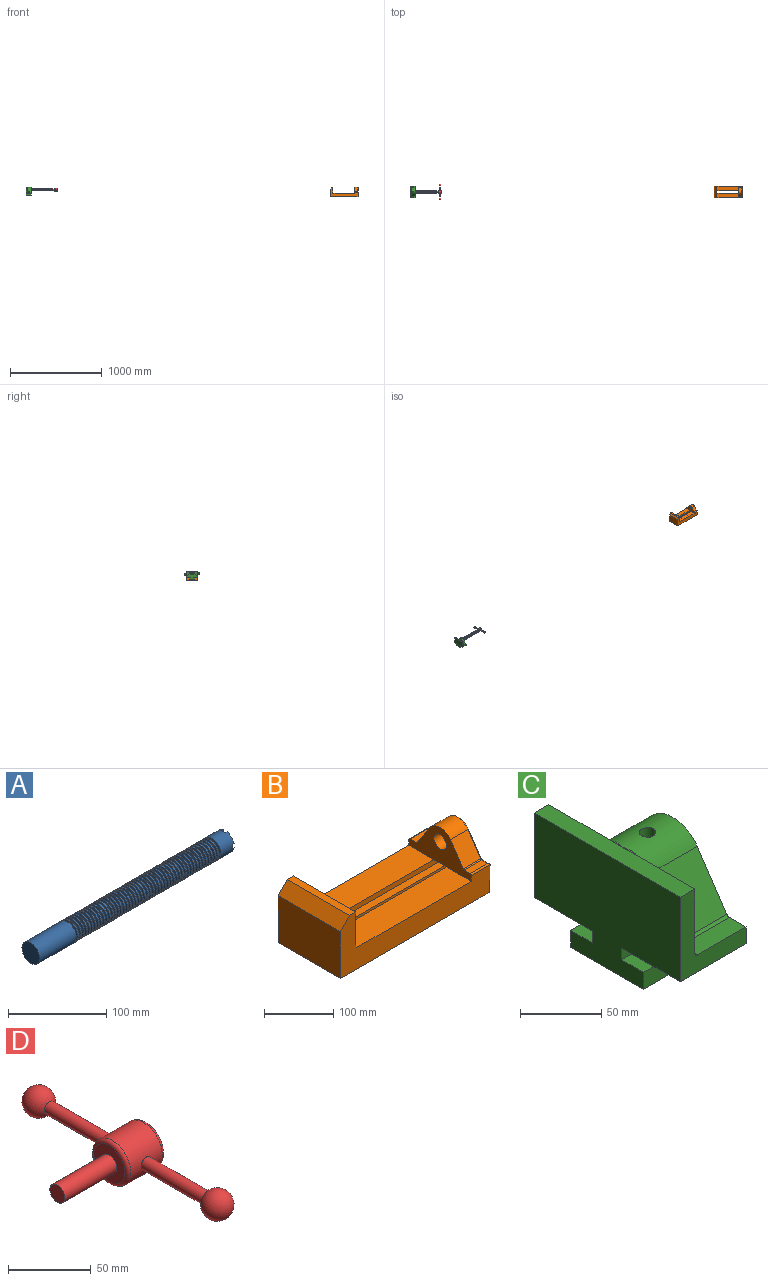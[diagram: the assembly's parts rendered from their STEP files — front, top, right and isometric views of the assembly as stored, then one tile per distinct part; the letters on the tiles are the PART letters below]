
ASSEMBLY  parts=4 mates=3
PART A: 220 faces, bbox 279.4x25.4x25.4 mm
  f0: cylinder r=12.7mm len=25.4mm, axis (-1,0,0), area 1468.2mm2, adj f1,f2,f3,f5,f7,f208,f209,f210
  f1: plane 9.9x9.9mm, normal (1,0,0), area 62.3mm2, adj f0,f4,f213,f216
  f2: plane 9.9x9.9mm, normal (1,0,0), area 62.3mm2, adj f0,f4,f210,f218
  f3: plane 9.9x9.9mm, normal (1,0,0), area 62.3mm2, adj f0,f4,f209,f212
  f4: cylinder r=6.35mm len=25.4mm, axis (1,0,0), area 960.3mm2, adj f1,f2,f3,f5,f6,f208,f209,f210
  f5: plane 9.9x9.9mm, normal (1,0,0), area 62.3mm2, adj f0,f4,f215,f217
  f6: plane 12.7x12.7mm, normal (1,0,0), area 126.7mm2, adj f4
  f7: cone r=12.7mm half-angle=76deg, axis (1,0,0), area 188mm2, adj f0,f9
  f8: cone r=10.16mm half-angle=76deg, axis (-1,0,0), area 188mm2, adj f9,f10
  f9: cylinder r=10.16mm len=20.32mm, axis (1,0,0), area 81.1mm2, adj f7,f8
  f10: cylinder r=12.7mm len=25.4mm, axis (-1,0,0), area 131.7mm2, adj f8,f11
  f11: cone r=12.7mm half-angle=76deg, axis (1,0,0), area 188mm2, adj f10,f13
  f12: cone r=10.16mm half-angle=76deg, axis (-1,0,0), area 188mm2, adj f13,f14
  f13: cylinder r=10.16mm len=20.32mm, axis (1,0,0), area 81.1mm2, adj f11,f12
  f14: cylinder r=12.7mm len=25.4mm, axis (-1,0,0), area 131.7mm2, adj f12,f15
  f15: cone r=12.7mm half-angle=76deg, axis (1,0,0), area 188mm2, adj f14,f17
  f16: cone r=10.16mm half-angle=76deg, axis (-1,0,0), area 188mm2, adj f17,f18
  f17: cylinder r=10.16mm len=20.32mm, axis (1,0,0), area 81.1mm2, adj f15,f16
  f18: cylinder r=12.7mm len=25.4mm, axis (-1,0,0), area 131.7mm2, adj f16,f19
  f19: cone r=12.7mm half-angle=76deg, axis (1,0,0), area 188mm2, adj f18,f21
  f20: cone r=10.16mm half-angle=76deg, axis (-1,0,0), area 188mm2, adj f21,f22
  f21: cylinder r=10.16mm len=20.32mm, axis (1,0,0), area 81.1mm2, adj f19,f20
  f22: cylinder r=12.7mm len=25.4mm, axis (-1,0,0), area 131.7mm2, adj f20,f23
  f23: cone r=12.7mm half-angle=76deg, axis (1,0,0), area 188mm2, adj f22,f25
  f24: cone r=10.16mm half-angle=76deg, axis (-1,0,0), area 188mm2, adj f25,f26
  f25: cylinder r=10.16mm len=20.32mm, axis (1,0,0), area 81.1mm2, adj f23,f24
  f26: cylinder r=12.7mm len=25.4mm, axis (-1,0,0), area 131.7mm2, adj f24,f27
  f27: cone r=12.7mm half-angle=76deg, axis (1,0,0), area 188mm2, adj f26,f29
  f28: cone r=10.16mm half-angle=76deg, axis (-1,0,0), area 188mm2, adj f29,f30
  f29: cylinder r=10.16mm len=20.32mm, axis (1,0,0), area 81.1mm2, adj f27,f28
  f30: cylinder r=12.7mm len=25.4mm, axis (-1,0,0), area 131.7mm2, adj f28,f31
  f31: cone r=12.7mm half-angle=76deg, axis (1,0,0), area 188mm2, adj f30,f33
  f32: cone r=10.16mm half-angle=76deg, axis (-1,0,0), area 188mm2, adj f33,f34
  f33: cylinder r=10.16mm len=20.32mm, axis (1,0,0), area 81.1mm2, adj f31,f32
  f34: cylinder r=12.7mm len=25.4mm, axis (-1,0,0), area 131.7mm2, adj f32,f35
  f35: cone r=12.7mm half-angle=76deg, axis (1,0,0), area 188mm2, adj f34,f37
  f36: cone r=10.16mm half-angle=76deg, axis (-1,0,0), area 188mm2, adj f37,f38
  f37: cylinder r=10.16mm len=20.32mm, axis (1,0,0), area 81.1mm2, adj f35,f36
  f38: cylinder r=12.7mm len=25.4mm, axis (-1,0,0), area 131.7mm2, adj f36,f39
  f39: cone r=12.7mm half-angle=76deg, axis (1,0,0), area 188mm2, adj f38,f41
  f40: cone r=10.16mm half-angle=76deg, axis (-1,0,0), area 188mm2, adj f41,f42
  f41: cylinder r=10.16mm len=20.32mm, axis (1,0,0), area 81.1mm2, adj f39,f40
  f42: cylinder r=12.7mm len=25.4mm, axis (-1,0,0), area 131.7mm2, adj f40,f43
  f43: cone r=12.7mm half-angle=76deg, axis (1,0,0), area 188mm2, adj f42,f45
  f44: cone r=10.16mm half-angle=76deg, axis (-1,0,0), area 188mm2, adj f45,f46
  f45: cylinder r=10.16mm len=20.32mm, axis (1,0,0), area 81.1mm2, adj f43,f44
  f46: cylinder r=12.7mm len=25.4mm, axis (-1,0,0), area 131.7mm2, adj f44,f47
  f47: cone r=12.7mm half-angle=76deg, axis (1,0,0), area 188mm2, adj f46,f49
  f48: cone r=10.16mm half-angle=76deg, axis (-1,0,0), area 188mm2, adj f49,f50
  f49: cylinder r=10.16mm len=20.32mm, axis (1,0,0), area 81.1mm2, adj f47,f48
  f50: cylinder r=12.7mm len=25.4mm, axis (-1,0,0), area 131.7mm2, adj f48,f51
  f51: cone r=12.7mm half-angle=76deg, axis (1,0,0), area 188mm2, adj f50,f53
  f52: cone r=10.16mm half-angle=76deg, axis (-1,0,0), area 188mm2, adj f53,f54
  f53: cylinder r=10.16mm len=20.32mm, axis (1,0,0), area 81.1mm2, adj f51,f52
  f54: cylinder r=12.7mm len=25.4mm, axis (-1,0,0), area 131.7mm2, adj f52,f55
  f55: cone r=12.7mm half-angle=76deg, axis (1,0,0), area 188mm2, adj f54,f57
  f56: cone r=10.16mm half-angle=76deg, axis (-1,0,0), area 188mm2, adj f57,f58
  f57: cylinder r=10.16mm len=20.32mm, axis (1,0,0), area 81.1mm2, adj f55,f56
  f58: cylinder r=12.7mm len=25.4mm, axis (-1,0,0), area 131.7mm2, adj f56,f59
  f59: cone r=12.7mm half-angle=76deg, axis (1,0,0), area 188mm2, adj f58,f61
  f60: cone r=10.16mm half-angle=76deg, axis (-1,0,0), area 188mm2, adj f61,f62
  f61: cylinder r=10.16mm len=20.32mm, axis (1,0,0), area 81.1mm2, adj f59,f60
  f62: cylinder r=12.7mm len=25.4mm, axis (-1,0,0), area 131.7mm2, adj f60,f63
  f63: cone r=12.7mm half-angle=76deg, axis (1,0,0), area 188mm2, adj f62,f65
  f64: cone r=10.16mm half-angle=76deg, axis (-1,0,0), area 188mm2, adj f65,f66
  f65: cylinder r=10.16mm len=20.32mm, axis (1,0,0), area 81.1mm2, adj f63,f64
  f66: cylinder r=12.7mm len=25.4mm, axis (-1,0,0), area 131.7mm2, adj f64,f67
  f67: cone r=12.7mm half-angle=76deg, axis (1,0,0), area 188mm2, adj f66,f69
  f68: cone r=10.16mm half-angle=76deg, axis (-1,0,0), area 188mm2, adj f69,f70
  f69: cylinder r=10.16mm len=20.32mm, axis (1,0,0), area 81.1mm2, adj f67,f68
  f70: cylinder r=12.7mm len=25.4mm, axis (-1,0,0), area 131.7mm2, adj f68,f71
  f71: cone r=12.7mm half-angle=76deg, axis (1,0,0), area 188mm2, adj f70,f73
  f72: cone r=10.16mm half-angle=76deg, axis (-1,0,0), area 188mm2, adj f73,f74
  f73: cylinder r=10.16mm len=20.32mm, axis (1,0,0), area 81.1mm2, adj f71,f72
  f74: cylinder r=12.7mm len=25.4mm, axis (-1,0,0), area 131.7mm2, adj f72,f75
  f75: cone r=12.7mm half-angle=76deg, axis (1,0,0), area 188mm2, adj f74,f77
  f76: cone r=10.16mm half-angle=76deg, axis (-1,0,0), area 188mm2, adj f77,f78
  f77: cylinder r=10.16mm len=20.32mm, axis (1,0,0), area 81.1mm2, adj f75,f76
  f78: cylinder r=12.7mm len=25.4mm, axis (-1,0,0), area 131.7mm2, adj f76,f79
  f79: cone r=12.7mm half-angle=76deg, axis (1,0,0), area 188mm2, adj f78,f81
  f80: cone r=10.16mm half-angle=76deg, axis (-1,0,0), area 188mm2, adj f81,f82
  f81: cylinder r=10.16mm len=20.32mm, axis (1,0,0), area 81.1mm2, adj f79,f80
  f82: cylinder r=12.7mm len=25.4mm, axis (-1,0,0), area 131.7mm2, adj f80,f83
  f83: cone r=12.7mm half-angle=76deg, axis (1,0,0), area 188mm2, adj f82,f85
  f84: cone r=10.16mm half-angle=76deg, axis (-1,0,0), area 188mm2, adj f85,f86
  f85: cylinder r=10.16mm len=20.32mm, axis (1,0,0), area 81.1mm2, adj f83,f84
  f86: cylinder r=12.7mm len=25.4mm, axis (-1,0,0), area 131.7mm2, adj f84,f87
  f87: cone r=12.7mm half-angle=76deg, axis (1,0,0), area 188mm2, adj f86,f89
  f88: cone r=10.16mm half-angle=76deg, axis (-1,0,0), area 188mm2, adj f89,f90
  f89: cylinder r=10.16mm len=20.32mm, axis (1,0,0), area 81.1mm2, adj f87,f88
  f90: cylinder r=12.7mm len=25.4mm, axis (-1,0,0), area 131.7mm2, adj f88,f91
  f91: cone r=12.7mm half-angle=76deg, axis (1,0,0), area 188mm2, adj f90,f93
  f92: cone r=10.16mm half-angle=76deg, axis (-1,0,0), area 188mm2, adj f93,f94
  f93: cylinder r=10.16mm len=20.32mm, axis (1,0,0), area 81.1mm2, adj f91,f92
  f94: cylinder r=12.7mm len=25.4mm, axis (-1,0,0), area 131.7mm2, adj f92,f95
  f95: cone r=12.7mm half-angle=76deg, axis (1,0,0), area 188mm2, adj f94,f97
  f96: cone r=10.16mm half-angle=76deg, axis (-1,0,0), area 188mm2, adj f97,f98
  f97: cylinder r=10.16mm len=20.32mm, axis (1,0,0), area 81.1mm2, adj f95,f96
  f98: cylinder r=12.7mm len=25.4mm, axis (-1,0,0), area 131.7mm2, adj f96,f99
  f99: cone r=12.7mm half-angle=76deg, axis (1,0,0), area 188mm2, adj f98,f101
  f100: cone r=10.16mm half-angle=76deg, axis (-1,0,0), area 188mm2, adj f101,f102
  f101: cylinder r=10.16mm len=20.32mm, axis (1,0,0), area 81.1mm2, adj f99,f100
  f102: cylinder r=12.7mm len=25.4mm, axis (-1,0,0), area 131.7mm2, adj f100,f103
  f103: cone r=12.7mm half-angle=76deg, axis (1,0,0), area 188mm2, adj f102,f105
  f104: cone r=10.16mm half-angle=76deg, axis (-1,0,0), area 188mm2, adj f105,f106
  f105: cylinder r=10.16mm len=20.32mm, axis (1,0,0), area 81.1mm2, adj f103,f104
  f106: cylinder r=12.7mm len=25.4mm, axis (-1,0,0), area 131.7mm2, adj f104,f107
  f107: cone r=12.7mm half-angle=76deg, axis (1,0,0), area 188mm2, adj f106,f109
  f108: cone r=10.16mm half-angle=76deg, axis (-1,0,0), area 188mm2, adj f109,f110
  f109: cylinder r=10.16mm len=20.32mm, axis (1,0,0), area 81.1mm2, adj f107,f108
  f110: cylinder r=12.7mm len=25.4mm, axis (-1,0,0), area 131.7mm2, adj f108,f111
  f111: cone r=12.7mm half-angle=76deg, axis (1,0,0), area 188mm2, adj f110,f113
  f112: cone r=10.16mm half-angle=76deg, axis (-1,0,0), area 188mm2, adj f113,f114
  f113: cylinder r=10.16mm len=20.32mm, axis (1,0,0), area 81.1mm2, adj f111,f112
  f114: cylinder r=12.7mm len=25.4mm, axis (-1,0,0), area 131.7mm2, adj f112,f115
  f115: cone r=12.7mm half-angle=76deg, axis (1,0,0), area 188mm2, adj f114,f117
  f116: cone r=10.16mm half-angle=76deg, axis (-1,0,0), area 188mm2, adj f117,f118
  f117: cylinder r=10.16mm len=20.32mm, axis (1,0,0), area 81.1mm2, adj f115,f116
  f118: cylinder r=12.7mm len=25.4mm, axis (-1,0,0), area 131.7mm2, adj f116,f119
  f119: cone r=12.7mm half-angle=76deg, axis (1,0,0), area 188mm2, adj f118,f121
  f120: cone r=10.16mm half-angle=76deg, axis (-1,0,0), area 188mm2, adj f121,f122
  f121: cylinder r=10.16mm len=20.32mm, axis (1,0,0), area 81.1mm2, adj f119,f120
  f122: cylinder r=12.7mm len=25.4mm, axis (-1,0,0), area 131.7mm2, adj f120,f123
  f123: cone r=12.7mm half-angle=76deg, axis (1,0,0), area 188mm2, adj f122,f125
  f124: cone r=10.16mm half-angle=76deg, axis (-1,0,0), area 188mm2, adj f125,f126
  f125: cylinder r=10.16mm len=20.32mm, axis (1,0,0), area 81.1mm2, adj f123,f124
  f126: cylinder r=12.7mm len=25.4mm, axis (-1,0,0), area 131.7mm2, adj f124,f127
  f127: cone r=12.7mm half-angle=76deg, axis (1,0,0), area 188mm2, adj f126,f129
  f128: cone r=10.16mm half-angle=76deg, axis (-1,0,0), area 188mm2, adj f129,f130
  f129: cylinder r=10.16mm len=20.32mm, axis (1,0,0), area 81.1mm2, adj f127,f128
  f130: cylinder r=12.7mm len=25.4mm, axis (-1,0,0), area 131.7mm2, adj f128,f131
  f131: cone r=12.7mm half-angle=76deg, axis (1,0,0), area 188mm2, adj f130,f133
  f132: cone r=10.16mm half-angle=76deg, axis (-1,0,0), area 188mm2, adj f133,f134
  f133: cylinder r=10.16mm len=20.32mm, axis (1,0,0), area 81.1mm2, adj f131,f132
  f134: cylinder r=12.7mm len=25.4mm, axis (-1,0,0), area 131.7mm2, adj f132,f135
  f135: cone r=12.7mm half-angle=76deg, axis (1,0,0), area 188mm2, adj f134,f137
  f136: cone r=10.16mm half-angle=76deg, axis (-1,0,0), area 188mm2, adj f137,f138
  f137: cylinder r=10.16mm len=20.32mm, axis (1,0,0), area 81.1mm2, adj f135,f136
  f138: cylinder r=12.7mm len=25.4mm, axis (-1,0,0), area 131.7mm2, adj f136,f139
  f139: cone r=12.7mm half-angle=76deg, axis (1,0,0), area 188mm2, adj f138,f141
  f140: cone r=10.16mm half-angle=76deg, axis (-1,0,0), area 188mm2, adj f141,f142
  f141: cylinder r=10.16mm len=20.32mm, axis (1,0,0), area 81.1mm2, adj f139,f140
  f142: cylinder r=12.7mm len=25.4mm, axis (-1,0,0), area 131.7mm2, adj f140,f143
  f143: cone r=12.7mm half-angle=76deg, axis (1,0,0), area 188mm2, adj f142,f145
  f144: cone r=10.16mm half-angle=76deg, axis (-1,0,0), area 188mm2, adj f145,f146
  f145: cylinder r=10.16mm len=20.32mm, axis (1,0,0), area 81.1mm2, adj f143,f144
  f146: cylinder r=12.7mm len=25.4mm, axis (-1,0,0), area 131.7mm2, adj f144,f147
  f147: cone r=12.7mm half-angle=76deg, axis (1,0,0), area 188mm2, adj f146,f149
  f148: cone r=10.16mm half-angle=76deg, axis (-1,0,0), area 188mm2, adj f149,f150
  f149: cylinder r=10.16mm len=20.32mm, axis (1,0,0), area 81.1mm2, adj f147,f148
  f150: cylinder r=12.7mm len=25.4mm, axis (-1,0,0), area 131.7mm2, adj f148,f151
  f151: cone r=12.7mm half-angle=76deg, axis (1,0,0), area 188mm2, adj f150,f153
  f152: cone r=10.16mm half-angle=76deg, axis (-1,0,0), area 188mm2, adj f153,f154
  f153: cylinder r=10.16mm len=20.32mm, axis (1,0,0), area 81.1mm2, adj f151,f152
  f154: cylinder r=12.7mm len=25.4mm, axis (-1,0,0), area 131.7mm2, adj f152,f155
  f155: cone r=12.7mm half-angle=76deg, axis (1,0,0), area 188mm2, adj f154,f157
  f156: cone r=10.16mm half-angle=76deg, axis (-1,0,0), area 188mm2, adj f157,f158
  f157: cylinder r=10.16mm len=20.32mm, axis (1,0,0), area 81.1mm2, adj f155,f156
  f158: cylinder r=12.7mm len=25.4mm, axis (-1,0,0), area 131.7mm2, adj f156,f159
  f159: cone r=12.7mm half-angle=76deg, axis (1,0,0), area 188mm2, adj f158,f161
  f160: cone r=10.16mm half-angle=76deg, axis (-1,0,0), area 188mm2, adj f161,f162
  f161: cylinder r=10.16mm len=20.32mm, axis (1,0,0), area 81.1mm2, adj f159,f160
  f162: cylinder r=12.7mm len=25.4mm, axis (-1,0,0), area 131.7mm2, adj f160,f163
  f163: cone r=12.7mm half-angle=76deg, axis (1,0,0), area 188mm2, adj f162,f165
  f164: cone r=10.16mm half-angle=76deg, axis (-1,0,0), area 188mm2, adj f165,f166
  f165: cylinder r=10.16mm len=20.32mm, axis (1,0,0), area 81.1mm2, adj f163,f164
  f166: cylinder r=12.7mm len=25.4mm, axis (-1,0,0), area 131.7mm2, adj f164,f167
  f167: cone r=12.7mm half-angle=76deg, axis (1,0,0), area 188mm2, adj f166,f169
  f168: cone r=10.16mm half-angle=76deg, axis (-1,0,0), area 188mm2, adj f169,f170
  f169: cylinder r=10.16mm len=20.32mm, axis (1,0,0), area 81.1mm2, adj f167,f168
  f170: cylinder r=12.7mm len=25.4mm, axis (-1,0,0), area 131.7mm2, adj f168,f171
  f171: cone r=12.7mm half-angle=76deg, axis (1,0,0), area 188mm2, adj f170,f173
  f172: cone r=10.16mm half-angle=76deg, axis (-1,0,0), area 188mm2, adj f173,f174
  f173: cylinder r=10.16mm len=20.32mm, axis (1,0,0), area 81.1mm2, adj f171,f172
  f174: cylinder r=12.7mm len=25.4mm, axis (-1,0,0), area 131.7mm2, adj f172,f175
  f175: cone r=12.7mm half-angle=76deg, axis (1,0,0), area 188mm2, adj f174,f177
  f176: cone r=10.16mm half-angle=76deg, axis (-1,0,0), area 188mm2, adj f177,f178
  f177: cylinder r=10.16mm len=20.32mm, axis (1,0,0), area 81.1mm2, adj f175,f176
  f178: cylinder r=12.7mm len=25.4mm, axis (-1,0,0), area 131.7mm2, adj f176,f179
  f179: cone r=12.7mm half-angle=76deg, axis (1,0,0), area 188mm2, adj f178,f181
  f180: cone r=10.16mm half-angle=76deg, axis (-1,0,0), area 188mm2, adj f181,f182
  f181: cylinder r=10.16mm len=20.32mm, axis (1,0,0), area 81.1mm2, adj f179,f180
  f182: cylinder r=12.7mm len=25.4mm, axis (-1,0,0), area 131.7mm2, adj f180,f183
  f183: cone r=12.7mm half-angle=76deg, axis (1,0,0), area 188mm2, adj f182,f185
  f184: cone r=10.16mm half-angle=76deg, axis (-1,0,0), area 188mm2, adj f185,f186
  f185: cylinder r=10.16mm len=20.32mm, axis (1,0,0), area 81.1mm2, adj f183,f184
  f186: cylinder r=12.7mm len=25.4mm, axis (-1,0,0), area 131.7mm2, adj f184,f187
  f187: cone r=12.7mm half-angle=76deg, axis (1,0,0), area 188mm2, adj f186,f189
  f188: cone r=10.16mm half-angle=76deg, axis (-1,0,0), area 188mm2, adj f189,f190
  f189: cylinder r=10.16mm len=20.32mm, axis (1,0,0), area 81.1mm2, adj f187,f188
  f190: cylinder r=12.7mm len=25.4mm, axis (-1,0,0), area 131.7mm2, adj f188,f191
  f191: cone r=12.7mm half-angle=76deg, axis (1,0,0), area 188mm2, adj f190,f193
  f192: cone r=10.16mm half-angle=76deg, axis (-1,0,0), area 188mm2, adj f193,f194
  f193: cylinder r=10.16mm len=20.32mm, axis (1,0,0), area 81.1mm2, adj f191,f192
  f194: cylinder r=12.7mm len=25.4mm, axis (-1,0,0), area 131.7mm2, adj f192,f195
  f195: cone r=12.7mm half-angle=76deg, axis (1,0,0), area 188mm2, adj f194,f197
  f196: cone r=10.16mm half-angle=76deg, axis (-1,0,0), area 188mm2, adj f197,f198
  f197: cylinder r=10.16mm len=20.32mm, axis (1,0,0), area 81.1mm2, adj f195,f196
  f198: cylinder r=12.7mm len=25.4mm, axis (-1,0,0), area 131.7mm2, adj f196,f199
  f199: cone r=12.7mm half-angle=76deg, axis (1,0,0), area 188mm2, adj f198,f201
  f200: cone r=10.16mm half-angle=76deg, axis (-1,0,0), area 188mm2, adj f201,f202
  f201: cylinder r=10.16mm len=20.32mm, axis (1,0,0), area 81.1mm2, adj f199,f200
  f202: cylinder r=12.7mm len=25.4mm, axis (-1,0,0), area 131.7mm2, adj f200,f203
  f203: cone r=12.7mm half-angle=76deg, axis (1,0,0), area 188mm2, adj f202,f205
  f204: cone r=10.16mm half-angle=76deg, axis (-1,0,0), area 188mm2, adj f205,f207
  f205: cylinder r=10.16mm len=20.32mm, axis (1,0,0), area 81.1mm2, adj f203,f204
  f206: plane 25.4x25.4mm, normal (-1,0,0), area 506.7mm2, adj f207
  f207: cylinder r=12.7mm len=52.45mm, axis (-1,0,0), area 4185.4mm2, adj f204,f206
  f208: plane 6.88x5.08mm, normal (1,0,0), area 32.7mm2, adj f0,f4,f209,f210
  f209: plane 6.62x2.54mm, normal (0,-1,0), area 16.8mm2, adj f0,f3,f4,f208
  f210: plane 6.62x2.54mm, normal (0,1,0), area 16.8mm2, adj f0,f2,f4,f208
  f211: plane 6.88x5.08mm, normal (1,0,0), area 32.7mm2, adj f0,f4,f212,f213
  f212: plane 6.62x2.54mm, normal (0,0,1), area 16.8mm2, adj f0,f3,f4,f211
  f213: plane 6.62x2.54mm, normal (0,0,-1), area 16.8mm2, adj f0,f1,f4,f211
  f214: plane 6.88x5.08mm, normal (1,0,0), area 32.7mm2, adj f0,f4,f215,f216
  f215: plane 6.62x2.54mm, normal (0,1,0), area 16.8mm2, adj f0,f4,f5,f214
  f216: plane 6.62x2.54mm, normal (0,-1,0), area 16.8mm2, adj f0,f1,f4,f214
  f217: plane 6.62x2.54mm, normal (0,0,-1), area 16.8mm2, adj f0,f4,f5,f219
  f218: plane 6.62x2.54mm, normal (0,0,1), area 16.8mm2, adj f0,f2,f4,f219
  f219: plane 6.88x5.08mm, normal (1,0,0), area 32.7mm2, adj f0,f4,f217,f218
PART B: 39 faces, bbox 304.8x127x103.7 mm
  f0: plane 234.95x50.8mm, normal (0,0,1), area 11935.5mm2, adj f2,f8,f16,f26
  f1: plane 234.95x50.8mm, normal (0,0,1), area 11935.5mm2, adj f2,f9,f16,f27
  f2: plane 127x101.6mm, normal (1,0,0), area 9516.1mm2, adj f0,f1,f3,f6,f8,f9,f18,f19
  f3: plane 127x12.7mm, normal (0,0,1), area 1612.9mm2, adj f2,f4,f8,f9
  f4: plane 127x19.05mm, normal (-0.71,0,0.71), area 3421.5mm2, adj f3,f5,f8,f9
  f5: plane 127x82.55mm, normal (-1,0,0), area 10483.9mm2, adj f4,f6,f8,f9
  f6: plane 304.8x127mm, normal (0,0,-1), area 31774.1mm2, adj f2,f5,f7,f8,f9,f21,f22
  f7: plane 127x99.06mm, normal (1,0,0), area 7097.5mm2, adj f6,f8,f9,f14,f17,f18,f19,f20
  f8: plane 304.8x101.6mm, normal (0,-1,0), area 13834.6mm2, adj f0,f2,f3,f4,f5,f6,f7,f16
  f9: plane 304.8x101.6mm, normal (0,1,0), area 13834.6mm2, adj f1,f2,f3,f4,f5,f6,f7,f16
  f10: plane 35.56x11.98mm, normal (0,0,1), area 426mm2, adj f16,f28,f29,f30
  f11: plane 38.43x35.56mm, normal (0,0.83,0.56), area 1645.4mm2, adj f12,f16,f29,f32
  f12: cylinder r=25.4mm len=42.19mm, axis (1,0,0), area 1770.2mm2, adj f11,f13,f16,f33
  f13: plane 38.43x35.56mm, normal (0,-0.83,0.56), area 1645.4mm2, adj f12,f16,f34,f35
  f14: cylinder r=12.7mm len=38.1mm, axis (1,0,0), area 3040.2mm2, adj f7,f16
  f15: plane 35.56x11.98mm, normal (0,0,1), area 426mm2, adj f16,f34,f36,f38
  f16: plane 127x63.5mm, normal (-1,0,0), area 4155.5mm2, adj f0,f1,f8,f9,f10,f11,f12,f13
  f17: plane 38.1x25.4mm, normal (0,0,-1), area 967.7mm2, adj f7,f16,f26,f27
  f18: plane 273.05x19.05mm, normal (0,0,-1), area 5201.6mm2, adj f2,f7,f19,f26
  f19: plane 273.05x12.7mm, normal (0,1,0), area 3467.7mm2, adj f2,f7,f18,f20
  f20: plane 273.05x19.05mm, normal (0,0,1), area 5201.6mm2, adj f2,f7,f19,f21
  f21: plane 273.05x16.51mm, normal (0,1,0), area 4508.1mm2, adj f2,f6,f7,f20
  f22: plane 273.05x16.51mm, normal (0,-1,0), area 4508.1mm2, adj f2,f6,f7,f23
  f23: plane 273.05x19.05mm, normal (0,0,1), area 5201.6mm2, adj f2,f7,f22,f24
  f24: plane 273.05x12.7mm, normal (0,-1,0), area 3467.7mm2, adj f2,f7,f23,f25
  f25: plane 273.05x19.05mm, normal (0,0,-1), area 5201.6mm2, adj f2,f7,f24,f27
  f26: plane 273.05x8.89mm, normal (0,1,0), area 2427.4mm2, adj f0,f2,f7,f17,f18
  f27: plane 273.05x8.89mm, normal (0,-1,0), area 2427.4mm2, adj f1,f2,f7,f17,f25
  f28: cylinder r=2.54mm len=38.1mm, axis (1,0,0), area 148.3mm2, adj f9,f10,f16,f30
  f29: cylinder r=2.54mm len=35.56mm, axis (-1,0,0), area 88.5mm2, adj f10,f11,f16,f31
  f30: cylinder r=2.54mm len=14.52mm, axis (0,1,0), area 54.3mm2, adj f7,f10,f28,f31
  f31: torus R=5.08mm, axis (-1,0,0), area 13.5mm2, adj f7,f29,f30,f32
  f32: cylinder r=2.54mm len=39.84mm, axis (0,0.56,-0.83), area 184.6mm2, adj f7,f11,f31,f33
  f33: torus R=22.86mm, axis (-1,0,0), area 191.4mm2, adj f7,f12,f32,f35
  f34: cylinder r=2.54mm len=35.56mm, axis (-1,0,0), area 88.5mm2, adj f13,f15,f16,f37
  f35: cylinder r=2.54mm len=39.84mm, axis (0,0.56,0.83), area 184.6mm2, adj f7,f13,f33,f37
  f36: cylinder r=2.54mm len=38.1mm, axis (-1,0,0), area 148.3mm2, adj f8,f15,f16,f38
  f37: torus R=5.08mm, axis (-1,0,0), area 13.5mm2, adj f7,f34,f35,f38
  f38: cylinder r=2.54mm len=14.52mm, axis (0,1,0), area 54.3mm2, adj f7,f15,f36,f37
PART C: 36 faces, bbox 57.2x127x89 mm
  f0: plane 57.15x50.8mm, normal (0,0,-1), area 2903.2mm2, adj f6,f9,f10,f23
  f1: cylinder r=12.7mm len=44.45mm, axis (1,0,0), area 3464.3mm2, adj f6,f15,f16
  f2: plane 41.91x14.52mm, normal (0,0,1), area 608.5mm2, adj f6,f11,f24,f25
  f3: plane 51.86x48.26mm, normal (1,0,0), area 1495.7mm2, adj f8,f10,f31,f33,f35
  f4: plane 51.86x48.26mm, normal (1,0,0), area 1495.7mm2, adj f8,f11,f24,f28,f29
  f5: plane 57.15x50.8mm, normal (0,0,-1), area 2903.2mm2, adj f6,f9,f11,f22
  f6: plane 127x85.09mm, normal (1,0,0), area 5190.6mm2, adj f0,f1,f2,f5,f7,f10,f11,f12
  f7: plane 41.91x14.52mm, normal (0,0,1), area 608.5mm2, adj f6,f10,f30,f31
  f8: plane 127x12.7mm, normal (0,0,1), area 1612.9mm2, adj f3,f4,f9,f10,f11,f26,f34
  f9: plane 127x85.09mm, normal (-1,0,0), area 9096.8mm2, adj f0,f5,f8,f10,f11,f17,f18,f19
  f10: plane 63.5x57.15mm, normal (0,-1,0), area 1372.3mm2, adj f0,f3,f6,f7,f8,f9,f31
  f11: plane 63.5x57.15mm, normal (0,1,0), area 1372.3mm2, adj f2,f4,f5,f6,f8,f9,f24
  f12: plane 41.91x38.43mm, normal (0,-0.83,0.56), area 1939.2mm2, adj f6,f13,f30,f33
  f13: cylinder r=25.4mm len=44.45mm, axis (1,0,0), area 2026.5mm2, adj f6,f12,f14,f16,f26,f28,f34,f35
  f14: plane 41.91x38.43mm, normal (0,0.83,0.56), area 1939.2mm2, adj f6,f13,f25,f29
  f15: plane 25.4x25.4mm, normal (1,0,0), area 506.7mm2, adj f1
  f16: cylinder r=5.08mm len=13.76mm, axis (0,0,1), area 414mm2, adj f1,f13
  f17: plane 57.15x19.05mm, normal (0,0,1), area 1088.7mm2, adj f6,f9,f18,f23
  f18: plane 57.15x12.7mm, normal (0,-1,0), area 725.8mm2, adj f6,f9,f17,f19
  f19: plane 63.5x57.15mm, normal (0,0,-1), area 3629mm2, adj f6,f9,f18,f20
  f20: plane 57.15x12.7mm, normal (0,1,0), area 725.8mm2, adj f6,f9,f19,f21
  f21: plane 57.15x19.05mm, normal (0,0,1), area 1088.7mm2, adj f6,f9,f20,f22
  f22: plane 57.15x8.89mm, normal (0,1,0), area 508.1mm2, adj f5,f6,f9,f21
  f23: plane 57.15x8.89mm, normal (0,-1,0), area 508.1mm2, adj f0,f6,f9,f17
  f24: cylinder r=2.54mm len=14.52mm, axis (0,-1,0), area 57.9mm2, adj f2,f4,f11,f27
  f25: cylinder r=2.54mm len=41.91mm, axis (1,0,0), area 104.3mm2, adj f2,f6,f14,f27
  f26: bspline ~12.24x2.8mm, area 20.9mm2, adj f8,f13,f28
  f27: sphere r=2.54mm, area 6.3mm2, adj f24,f25,f29
  f28: torus R=27.94mm, axis (1,0,0), area 57.8mm2, adj f4,f13,f26,f29
  f29: cylinder r=2.54mm len=39.84mm, axis (0,-0.56,0.83), area 184.6mm2, adj f4,f14,f27,f28
  f30: cylinder r=2.54mm len=41.91mm, axis (1,0,0), area 104.3mm2, adj f6,f7,f12,f32
  f31: cylinder r=2.54mm len=14.52mm, axis (0,-1,0), area 57.9mm2, adj f3,f7,f10,f32
  f32: sphere r=2.54mm, area 6.3mm2, adj f30,f31,f33
  f33: cylinder r=2.54mm len=39.84mm, axis (0,-0.56,-0.83), area 184.6mm2, adj f3,f12,f32,f35
  f34: bspline ~12.24x2.8mm, area 20.9mm2, adj f8,f13,f35
  f35: torus R=27.94mm, axis (1,0,0), area 57.8mm2, adj f3,f13,f33,f34
PART D: 11 faces, bbox 76.2x172.7x34.4 mm
  f0: sphere r=10.16mm, area 1231.8mm2, adj f1
  f1: cylinder r=4.45mm len=51.82mm, axis (0,1,0), area 1438.5mm2, adj f0,f4
  f2: sphere r=10.16mm, area 1231.8mm2, adj f3
  f3: cylinder r=4.45mm len=51.82mm, axis (0,1,0), area 1438.5mm2, adj f2,f4
  f4: cylinder r=15.88mm len=31.75mm, axis (-1,0,0), area 2534.7mm2, adj f1,f3,f9,f10
  f5: cylinder r=6.35mm len=44.45mm, axis (-1,0,0), area 1773.5mm2, adj f6,f8
  f6: plane 12.7x12.7mm, normal (-1,0,0), area 126.7mm2, adj f5
  f7: plane 26.67x26.67mm, normal (1,0,0), area 558.6mm2, adj f10
  f8: plane 26.67x26.67mm, normal (-1,0,0), area 432mm2, adj f5,f9
  f9: torus R=13.33mm, axis (1,0,0), area 374.8mm2, adj f4,f8
  f10: torus R=13.33mm, axis (1,0,0), area 374.8mm2, adj f4,f7
PLACE A rot(axis=(-1,0,0),4.6deg) t=(-3348.33,-6.1,0.24)mm
PLACE B at identity fixed
PLACE C t=(-3348.33,0,0)mm
PLACE D rot(axis=(-1,0,0),4.6deg) t=(-3348.33,-6.1,0.24)mm
MATE fastened A.f4 <-> D.f5  axis (1,0,0) through (-3354.68,0,76.2)mm
MATE revolute C.f28 <-> A.f7  axis (1,0,0) through (-3608.68,0,76.2)mm
MATE slider B.f2 <-> C.f9  axis (-1,0,0) through (-273.05,-63.5,38.1)mm
